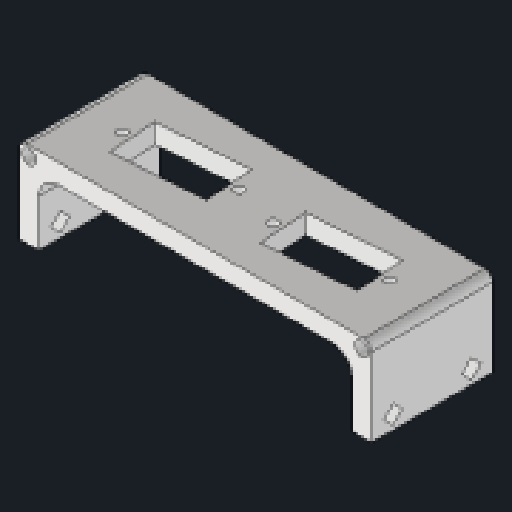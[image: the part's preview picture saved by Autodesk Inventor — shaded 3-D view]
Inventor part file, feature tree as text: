
AUTODESK INVENTOR PART (.ipt)
format: ipt  version: 2023.2 (Build 272271030, 271C)  size: 209,408 bytes
history: native  units: mm
features: sketch x5, projected_geometry x4, extrude x3, hole x2, other x2, fillet x2, mirror x1
ambient origin geometry x8: Origin, YZ Plane, XZ Plane, XY Plane, X Axis, Y Axis, Z Axis, Center Point
bodies: Solid1 (feature_tree)
feature tree (19):
  extrude  "Extrusion1"  Depth=5.0mm
  extrude  "Extrusion2"  Depth=32.0mm TaperAngle=0.0deg
  hole  "Hole1"  [1 undecoded]
  extrude  "Extrusion3"  Depth=10.0mm
  other  "Work Axis1"
  other  "Work Axis2"
  hole  "Hole2"  [1 undecoded]
  mirror  "Mirror1"
  fillet  "Fillet1"  Radius=12.0mm
  fillet  "Fillet2"  Radius=27.8mm
  sketch  "Sketch1"  dims[d0=5.0mm d1=80.0mm]
  sketch  "Sketch2"  dims[d2=22.0mm d3=32.0mm d4=0.0mm]
  sketch  "Sketch3"  dims[d5=3.4mm d6=20.0mm]
  projected_geometry  "Projected Loop1"
  sketch  "Sketch4"  dims[d7=18.5mm d8=10.0mm]
  projected_geometry  "Projected Loop2"
  sketch  "Sketch5"  dims[d9=0.0mm d10=0.0mm d11=5.0mm d12=12.0mm d13=27.8mm d14=19.05mm d15=19.05mm d16=32.0mm d17=11.61895mm d18=5.809475mm d19=3.0mm d20=2.5mm d21=6.0mm d22=3.7mm d23=4.0mm d24=90.0deg d25=8.0mm d26=20.594885mm d27=23.0mm d28=12.5mm d29=0.0mm d30=0.0mm d31=2.5mm d32=2.5mm d33=2.5mm d34=3.7mm d35=6.0mm d36=4.0mm d37=2.0mm d38=90.0deg d39=3.5mm d40=0.0mm d41=2.0mm d42=5.0mm d43=1.0mm d44=1.0mm d45=1.0mm d46=4.0mm d47=2.5mm d48=3.7mm d49=14.3117mm d50=0.75mm d51=20.594885mm d52=0.0625mm d53=0.75mm d54=0.375mm]
  projected_geometry  "Projected Loop3"
  projected_geometry  "Projected Loop4"
note: 2 required parameter values undecoded (feature->parameter linkage not recoverable at this tier; creation-order binding heuristic only, values carry confidence <= 0.55)
